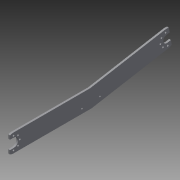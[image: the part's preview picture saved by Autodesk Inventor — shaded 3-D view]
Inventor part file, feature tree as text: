
AUTODESK INVENTOR PART (.ipt)
format: ipt  version: 2013 (Build 170138000, 138)  size: 143,360 bytes
history: native  units: mm
features: sketch x3, hole x2, pattern_circular x2, other x1, extrude x1
ambient origin geometry x8: Origin, YZ Plane, XZ Plane, XY Plane, X Axis, Y Axis, Z Axis, Center Point
feature tree (9):
  other  "ソリッド1"
  extrude  "押し出し1"  Depth=20.0mm
  hole  "穴1"  [1 undecoded]
  pattern_circular  "円形状パターン1"  [2 undecoded]
  pattern_circular  "円形状パターン2"  [2 undecoded]
  hole  "穴2"  [1 undecoded]
  sketch  "スケッチ2"
  sketch  "スケッチ3"
  sketch  "スケッチ4"
note: 6 required parameter values undecoded (feature->parameter linkage not recoverable at this tier; creation-order binding heuristic only, values carry confidence <= 0.55)
